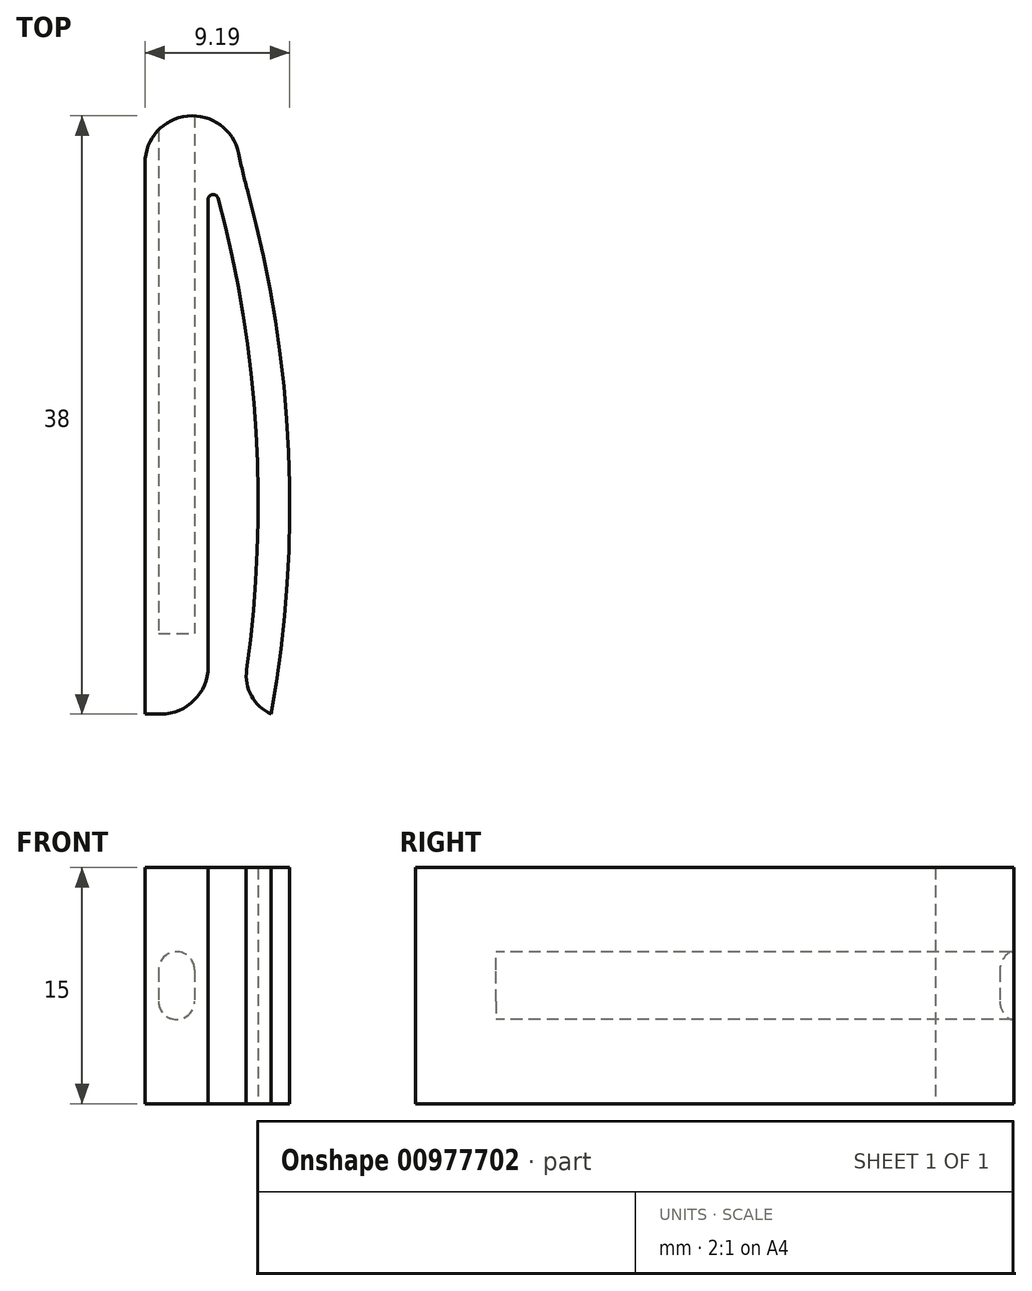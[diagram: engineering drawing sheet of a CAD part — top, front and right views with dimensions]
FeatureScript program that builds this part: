
annotation { "Feature Type Name" : "Feature", "Feature Type Description" : "" }
export const myFeature = defineFeature(function(context is Context, id is Id, definition is map)
    precondition{}
    {
        {
            var Q0;
            Q0=qCreatedBy(makeId("Top.planeOp"),FACE);
            var sketch = newSketch(context, id + "F0", { "sketchPlane" : qUnion([Q0])});
            skLineSegment(sketch, "E0", {"start": v(0, 0) * mm, "end": v(-4, 0) * mm});
            skLineSegment(sketch, "E1", {"start": v(-4, 0) * mm, "end": v(-4, 35) * mm});
            skLineSegment(sketch, "E2", {"start": v(-4, 35) * mm, "end": v(0, 35) * mm});
            skLineSegment(sketch, "E3", {"start": v(0, 35) * mm, "end": v(0, 0) * mm});
            skLineSegment(sketch, "E4", {"start": v(0, 0) * mm, "end": v(2, 0) * mm, "construction": true});
            skArc(sketch, "E5", {"start": v(2, 0) * mm, "mid": v(3.06, 17.62) * mm, "end": v(0, 35) * mm});
            skLineSegment(sketch, "E6", {"start": v(0, 35) * mm, "end": v(2, 35) * mm, "construction": true});
            skLineSegment(sketch, "E7", {"start": v(2, 0) * mm, "end": v(4, 0) * mm, "construction": true});
            skLineSegment(sketch, "E8", {"start": v(3.06, 17.62) * mm, "end": v(5.06, 17.62) * mm, "construction": true});
            skArc(sketch, "E9", {"start": v(4, 0) * mm, "mid": v(5.06, 17.62) * mm, "end": v(2, 35) * mm});
            skArc(sketch, "E10", {"start": v(2, 35) * mm, "mid": v(-1, 38) * mm, "end": v(-4, 35) * mm});
            skLineSegment(sketch, "E11", {"start": v(4, 0) * mm, "end": v(2, 0) * mm});
            skSolve(sketch);
        }
        {
            var Q0;
            Q0=makeQuery(id+"F0.imprint","IMPRINT",FACE,{"disambiguationData":[TD([[makeQuery(id+"F0.imprint","IMPRINT",EDGE,{"derivedFrom":sQuery(id+"F0.wireOp",EDGE,"E0")}),-1.0]])]});
            var Q1;
            Q1=makeQuery(id+"F0.imprint","IMPRINT",FACE,{"disambiguationData":[TD([[makeQuery(id+"F0.imprint","IMPRINT",EDGE,{"derivedFrom":sQuery(id+"F0.wireOp",EDGE,"E2")}),1.0]])]});
            extrude(context, id + "F1", {"entities" : qUnion([Q0, Q1]), "depth" : 15 * mm, "offsetDistance" : 25 * mm});
        }
        {
            var Q0;
            Q0=makeQuery(id+"F1.opExtrude","SWEPT_EDGE",EDGE,{"disambiguationData":[OSD([sQuery(id+"F0.wireOp",EDGE,"E2"),sQuery(id+"F0.wireOp",EDGE,"E3"),sQuery(id+"F0.wireOp",EDGE,"E5")])]});
            fillet(context, id + "F2", {"entities" : qUnion([Q0]), "radius" : 0.32 * mm, "tangentPropagation" : true, "allowEdgeOverflow" : false});
        }
        {
            var Q0;
            Q0=makeQuery(id+"F1.opExtrude","SWEPT_EDGE",EDGE,{"disambiguationData":[OSD([sQuery(id+"F0.wireOp",EDGE,"E5"),sQuery(id+"F0.wireOp",EDGE,"E11")])]});
            fillet(context, id + "F3", {"entities" : qUnion([Q0]), "radius" : 2.69 * mm, "tangentPropagation" : true, "allowEdgeOverflow" : false});
        }
        {
            var Q0;
            Q0=makeQuery(id+"F1.opExtrude","SWEPT_FACE",FACE,{"disambiguationData":[OSD([sQuery(id+"F0.wireOp",EDGE,"E0")])]});
            var sketch = newSketch(context, id + "F4", { "sketchPlane" : qUnion([Q0])});
            skLineSegment(sketch, "E12", {"start": v(-4, 7.5) * mm, "end": v(0, 7.5) * mm, "construction": true});
            skLineSegment(sketch, "E13", {"start": v(-2, 7.5) * mm, "end": v(-2, 8.5) * mm, "construction": true});
            skLineSegment(sketch, "E14", {"start": v(-2, 7.5) * mm, "end": v(-2, 6.5) * mm, "construction": true});
            skCircle(sketch, "E15", {"center": v(-2, 8.5) * mm, "radius": 1.15 * mm});
            skArc(sketch, "E16", {"start": v(-2.57, 7.5) * mm, "mid": v(-2, 5.35) * mm, "end": v(-1.43, 7.5) * mm});
            skLineSegment(sketch, "E17", {"start": v(-2, 6.5) * mm, "end": v(-0.85, 6.5) * mm});
            skLineSegment(sketch, "E18", {"start": v(-2, 8.5) * mm, "end": v(-0.85, 8.5) * mm});
            skLineSegment(sketch, "E19", {"start": v(-0.85, 8.5) * mm, "end": v(-0.85, 6.5) * mm});
            skLineSegment(sketch, "E20", {"start": v(-2, 8.5) * mm, "end": v(-3.15, 8.5) * mm});
            skLineSegment(sketch, "E21", {"start": v(-2, 6.5) * mm, "end": v(-3.15, 6.5) * mm});
            skLineSegment(sketch, "E22", {"start": v(-3.15, 6.5) * mm, "end": v(-3.15, 8.5) * mm});
            skSolve(sketch);
        }
        {
            var Q0;
            {var subQ0=sQuery(id+"F4.wireOp",EDGE,"E17");Q0=makeQuery(id+"F4.imprint","IMPRINT",FACE,{"disambiguationData":[TD([[makeQuery(id+"F4.imprint","IMPRINT",EDGE,{"derivedFrom":subQ0}),-1.0]])]});}
            var Q1;
            {var subQ3=sQuery(id+"F4.wireOp",EDGE,"E17");Q1=makeQuery(id+"F4.imprint","IMPRINT",FACE,{"disambiguationData":[TD([[makeQuery(id+"F4.imprint","IMPRINT",EDGE,{"derivedFrom":subQ3}),1.0]])]});}
            var Q2;
            {var subQ3=sQuery(id+"F4.wireOp",EDGE,"E22");Q2=makeQuery(id+"F4.imprint","IMPRINT",FACE,{"disambiguationData":[TD([[makeQuery(id+"F4.imprint","IMPRINT",EDGE,{"derivedFrom":subQ3}),-1.0]])]});}
            var Q3;
            {var subQ3=sQuery(id+"F4.wireOp",EDGE,"E19");Q3=makeQuery(id+"F4.imprint","IMPRINT",FACE,{"disambiguationData":[TD([[makeQuery(id+"F4.imprint","IMPRINT",EDGE,{"derivedFrom":subQ3}),-1.0]])]});}
            var Q4;
            {var subQ0=sQuery(id+"F4.wireOp",EDGE,"E18");Q4=makeQuery(id+"F4.imprint","IMPRINT",FACE,{"disambiguationData":[TD([[makeQuery(id+"F4.imprint","IMPRINT",EDGE,{"derivedFrom":subQ0}),-1.0]])]});}
            var Q5;
            {var subQ0=sQuery(id+"F4.wireOp",EDGE,"E18");Q5=makeQuery(id+"F4.imprint","IMPRINT",FACE,{"disambiguationData":[TD([[makeQuery(id+"F4.imprint","IMPRINT",EDGE,{"derivedFrom":subQ0}),1.0]])]});}
            extrude(context, id + "F5", {"entities" : qUnion([Q0, Q1, Q2, Q3, Q4, Q5]), "operationType" : NewBodyOperationType.REMOVE, "oppositeDirection" : true, "depth" : 47 * mm, "offsetDistance" : 25 * mm});
        }
        {
            var Q0;
            {var subQ0=sQuery(id+"F4.wireOp",EDGE,"E18");Q0=makeQuery(id+"F4.imprint","IMPRINT",FACE,{"disambiguationData":[TD([[makeQuery(id+"F4.imprint","IMPRINT",EDGE,{"derivedFrom":subQ0}),1.0]])]});}
            var Q1;
            {var subQ0=sQuery(id+"F4.wireOp",EDGE,"E18");Q1=makeQuery(id+"F4.imprint","IMPRINT",FACE,{"disambiguationData":[TD([[makeQuery(id+"F4.imprint","IMPRINT",EDGE,{"derivedFrom":subQ0}),-1.0]])]});}
            var Q2;
            {var subQ0=sQuery(id+"F4.wireOp",EDGE,"E17");Q2=makeQuery(id+"F4.imprint","IMPRINT",FACE,{"disambiguationData":[TD([[makeQuery(id+"F4.imprint","IMPRINT",EDGE,{"derivedFrom":subQ0}),-1.0]])]});}
            var Q3;
            {var subQ3=sQuery(id+"F4.wireOp",EDGE,"E17");Q3=makeQuery(id+"F4.imprint","IMPRINT",FACE,{"disambiguationData":[TD([[makeQuery(id+"F4.imprint","IMPRINT",EDGE,{"derivedFrom":subQ3}),1.0]])]});}
            var Q4;
            {var subQ3=sQuery(id+"F4.wireOp",EDGE,"E19");Q4=makeQuery(id+"F4.imprint","IMPRINT",FACE,{"disambiguationData":[TD([[makeQuery(id+"F4.imprint","IMPRINT",EDGE,{"derivedFrom":subQ3}),-1.0]])]});}
            var Q5;
            {var subQ3=sQuery(id+"F4.wireOp",EDGE,"E22");Q5=makeQuery(id+"F4.imprint","IMPRINT",FACE,{"disambiguationData":[TD([[makeQuery(id+"F4.imprint","IMPRINT",EDGE,{"derivedFrom":subQ3}),-1.0]])]});}
            extrude(context, id + "F6", {"entities" : qUnion([Q0, Q1, Q2, Q3, Q4, Q5]), "operationType" : NewBodyOperationType.ADD, "oppositeDirection" : true, "depth" : 5.1 * mm, "offsetDistance" : 25 * mm});
        }
        {
            var Q0;
            Q0=makeQuery(id+"F1.opExtrude","SWEPT_EDGE",EDGE,{"disambiguationData":[OSD([sQuery(id+"F0.wireOp",EDGE,"E0"),sQuery(id+"F0.wireOp",EDGE,"E3")])]});
            fillet(context, id + "F7", {"entities" : qUnion([Q0]), "radius" : 3 * mm, "tangentPropagation" : true, "allowEdgeOverflow" : false});
        }
        {
            var Q0;
            Q0=makeQuery(id+"F1.opExtrude","SWEPT_EDGE",EDGE,{"disambiguationData":[OSD([sQuery(id+"F0.wireOp",EDGE,"E9"),sQuery(id+"F0.wireOp",EDGE,"E10")])]});
            fillet(context, id + "F8", {"entities" : qUnion([Q0]), "radius" : 43.77 * mm, "tangentPropagation" : true, "allowEdgeOverflow" : false});
        }
    });
